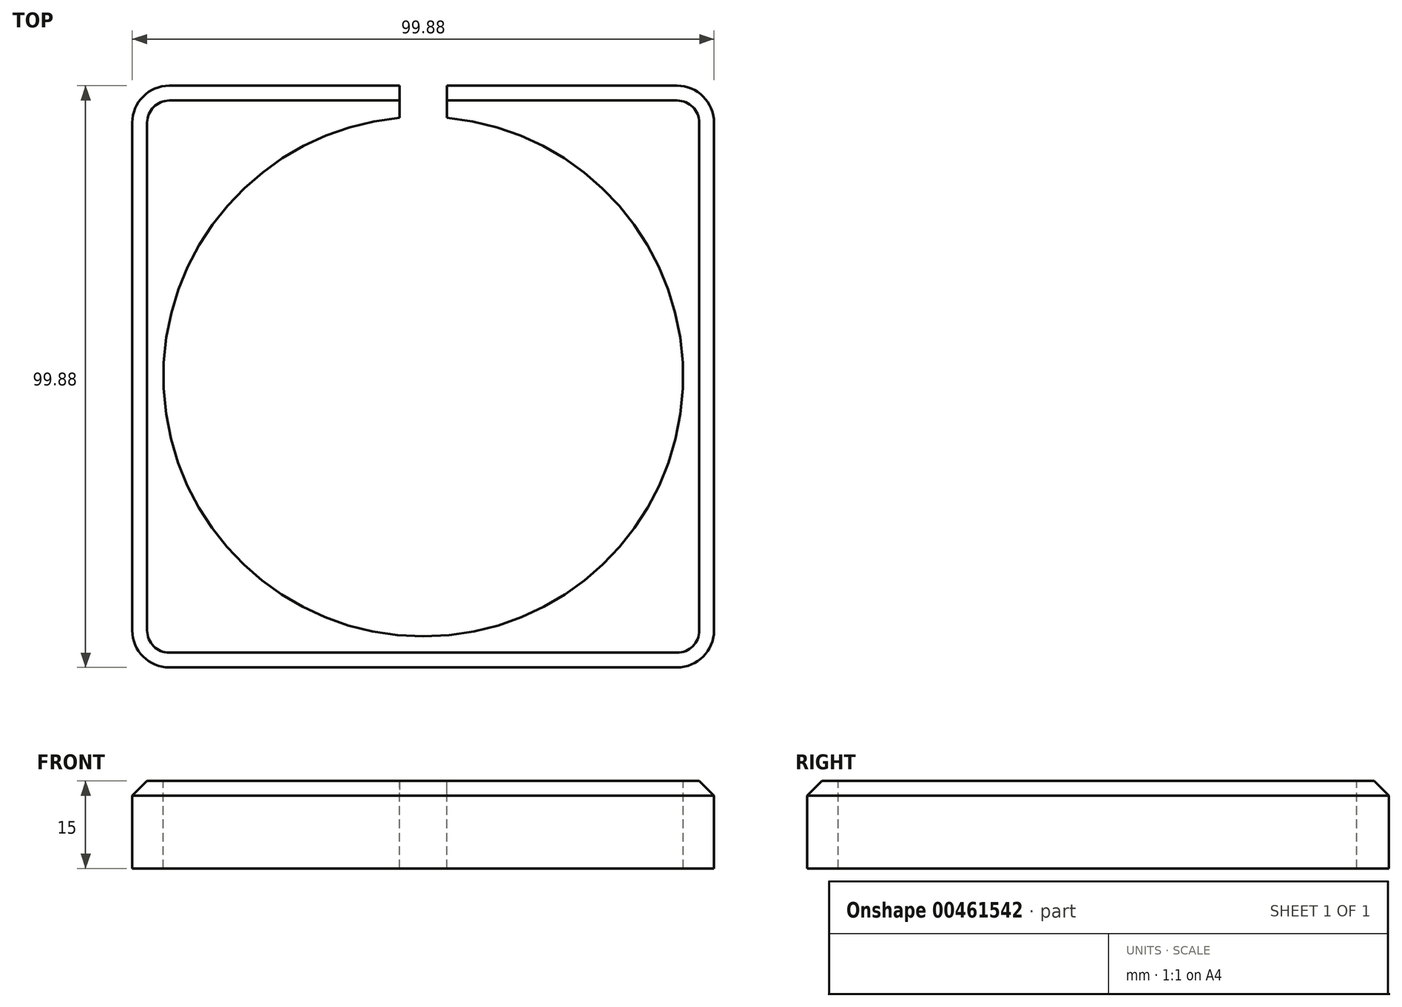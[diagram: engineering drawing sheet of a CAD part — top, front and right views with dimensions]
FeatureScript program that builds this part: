
annotation { "Feature Type Name" : "Feature", "Feature Type Description" : "" }
export const myFeature = defineFeature(function(context is Context, id is Id, definition is map)
    precondition{}
    {
        {
            var Q0;
            Q0=qCreatedBy(makeId("Top.planeOp"),FACE);
            var sketch = newSketch(context, id + "F0", { "sketchPlane" : qUnion([Q0])});
            skLineSegment(sketch, "E0.bottom", {"start": v(43.57, -49.94) * mm, "end": v(-43.6, -49.94) * mm});
            skLineSegment(sketch, "E0.top", {"start": v(43.57, 49.94) * mm, "end": v(-43.6, 49.94) * mm});
            skLineSegment(sketch, "E0.left", {"start": v(49.92, -43.59) * mm, "end": v(49.92, 43.59) * mm});
            skLineSegment(sketch, "E0.right", {"start": v(-49.96, -43.59) * mm, "end": v(-49.96, 43.59) * mm});
            skPoint(sketch, "E0.middle", {"position": v(-0.02, 0) * mm});
            skPoint(sketch, "E1.visualSharp", {"position": v(-49.96, -49.94) * mm});
            skArc(sketch, "E1.filletArc", {"start": v(-49.96, -43.59) * mm, "mid": v(-48.1, -48.08) * mm, "end": v(-43.6, -49.94) * mm});
            skPoint(sketch, "E2.visualSharp", {"position": v(-49.96, 49.94) * mm});
            skArc(sketch, "E2.filletArc", {"start": v(-43.6, 49.94) * mm, "mid": v(-48.1, 48.08) * mm, "end": v(-49.96, 43.59) * mm});
            skPoint(sketch, "E3.visualSharp", {"position": v(49.92, -49.94) * mm});
            skArc(sketch, "E3.filletArc", {"start": v(43.57, -49.94) * mm, "mid": v(48.06, -48.08) * mm, "end": v(49.92, -43.59) * mm});
            skPoint(sketch, "E4.visualSharp", {"position": v(49.92, 49.94) * mm});
            skArc(sketch, "E4.filletArc", {"start": v(49.92, 43.59) * mm, "mid": v(48.06, 48.08) * mm, "end": v(43.57, 49.94) * mm});
            skCircle(sketch, "E5", {"center": v(0, 0) * mm, "radius": 44.61 * mm});
            skLineSegment(sketch, "E6.bottom", {"start": v(-4.05, 61.67) * mm, "end": v(4.05, 61.67) * mm});
            skLineSegment(sketch, "E6.top", {"start": v(-4.05, 13.03) * mm, "end": v(4.05, 13.03) * mm});
            skLineSegment(sketch, "E6.left", {"start": v(-4.05, 61.67) * mm, "end": v(-4.05, 13.03) * mm});
            skLineSegment(sketch, "E6.right", {"start": v(4.05, 61.67) * mm, "end": v(4.05, 13.03) * mm});
            skPoint(sketch, "E6.middle", {"position": v(0, 37.35) * mm});
            skSolve(sketch);
        }
        {
            var Q0;
            Q0=makeQuery(id+"F0.imprint","IMPRINT",FACE,{"disambiguationData":[TD([[makeQuery(id+"F0.imprint","IMPRINT",EDGE,{"derivedFrom":sQuery(id+"F0.wireOp",EDGE,"E0.bottom")}),-1.0]])]});
            extrude(context, id + "F1", {"entities" : qUnion([Q0]), "oppositeDirection" : true, "depth" : 15 * mm});
        }
        {
            var Q0;
            Q0=makeQuery(id+"F1.opExtrude","CAP_EDGE",EDGE,{"disambiguationData":[OSD([sQuery(id+"F0.wireOp",EDGE,"E0.right")])],"isStart":true});
            chamfer(context, id + "F2", {"entities" : qUnion([Q0]), "width" : 2.54 * mm, "tangentPropagation" : true});
        }
    });
